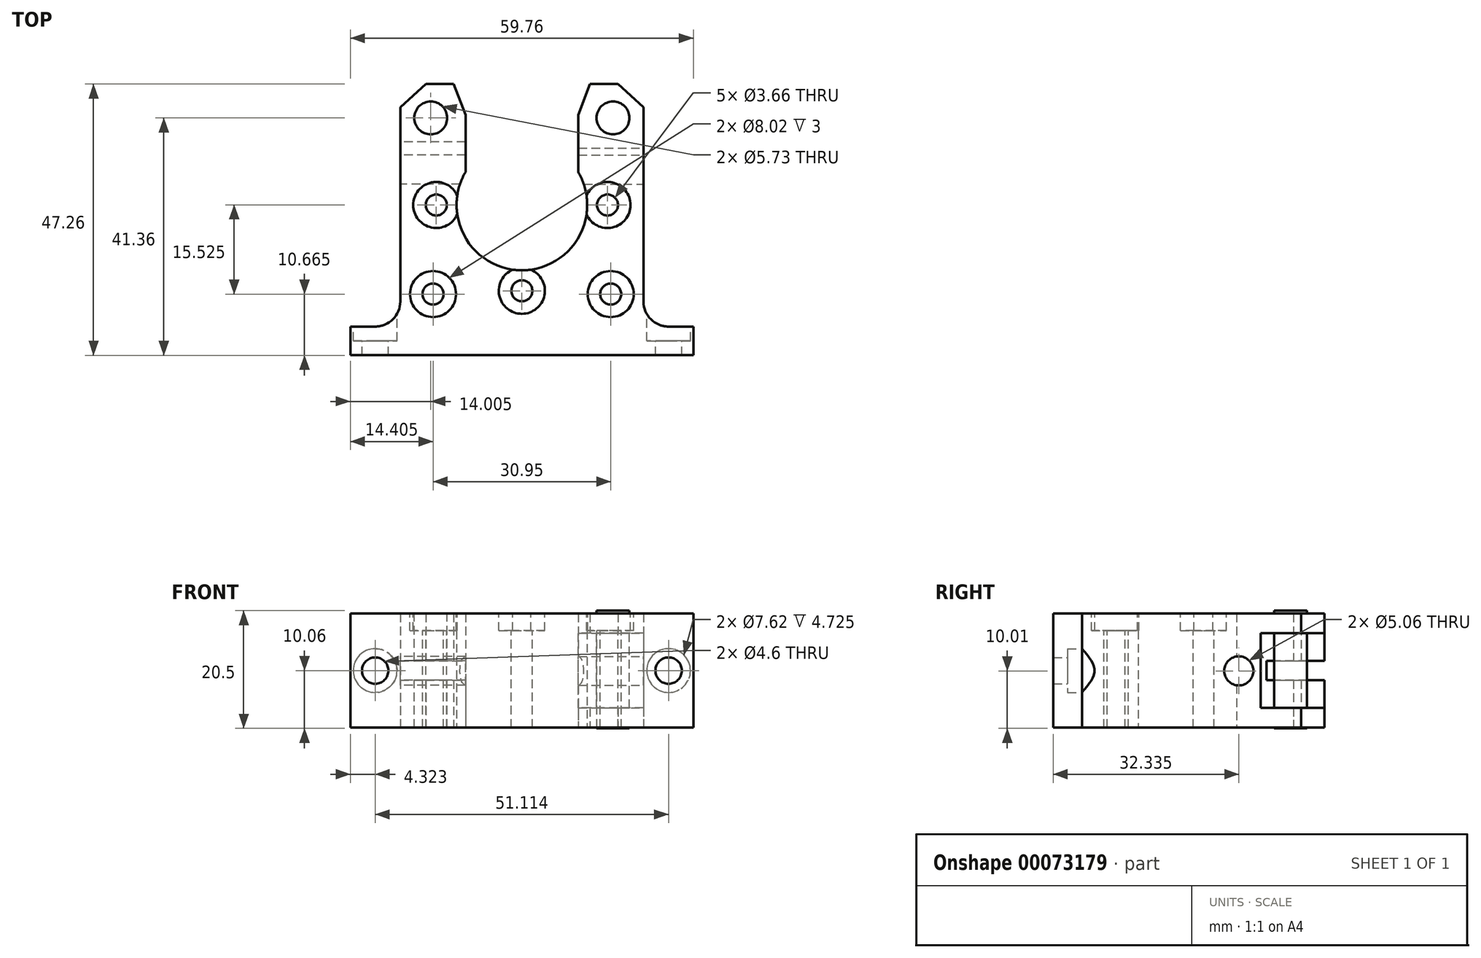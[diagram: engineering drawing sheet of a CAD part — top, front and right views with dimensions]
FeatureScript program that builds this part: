
annotation { "Feature Type Name" : "Feature", "Feature Type Description" : "" }
export const myFeature = defineFeature(function(context is Context, id is Id, definition is map)
    precondition{}
    {
        {
            var Q0;
            Q0=qCreatedBy(makeId("Top.planeOp"),FACE);
            var sketch = newSketch(context, id + "F0", { "sketchPlane" : qUnion([Q0])});
            skLineSegment(sketch, "E0", {"start": v(0, -26.18) * mm, "end": v(29.88, -26.18) * mm});
            skLineSegment(sketch, "E1", {"start": v(29.88, -26.18) * mm, "end": v(29.88, -21.18) * mm});
            skLineSegment(sketch, "E2", {"start": v(29.88, -21.18) * mm, "end": v(21.18, -21.18) * mm});
            skLineSegment(sketch, "E3", {"start": v(21.18, -21.18) * mm, "end": v(21.18, 17.02) * mm});
            skLineSegment(sketch, "E4", {"start": v(21.18, 17.02) * mm, "end": v(16.73, 21.07) * mm});
            skLineSegment(sketch, "E5", {"start": v(16.73, 21.07) * mm, "end": v(11.88, 21.07) * mm});
            skLineSegment(sketch, "E6", {"start": v(11.88, 21.07) * mm, "end": v(9.82, 15.68) * mm});
            skLineSegment(sketch, "E7", {"start": v(9.83, 15.68) * mm, "end": v(9.83, 5.73) * mm});
            skArc(sketch, "E8", {"start": v(0, -11.38) * mm, "mid": v(9.86, -5.67) * mm, "end": v(9.83, 5.73) * mm});
            skPoint(sketch, "E9", {"position": v(9.83, 5.73) * mm});
            skPoint(sketch, "E10", {"position": v(9.83, -5.73) * mm});
            skPoint(sketch, "E11.end.orphan", {"position": v(0, -11.38) * mm});
            skLineSegment(sketch, "E12", {"start": v(0, -11.38) * mm, "end": v(0, -26.18) * mm});
            skSolve(sketch);
        }
        {
            var Q0;
            Q0 = qSketchRegion(id + "F0", true);
            extrude(context, id + "F1", {"entities" : qUnion([Q0]), "depth" : 19.88 * mm});
        }
        {
            var Q0;
            Q0=makeQuery(id+"F1.opExtrude","SWEPT_EDGE",EDGE,{"disambiguationData":[OSD([sQuery(id+"F0.wireOp",EDGE,"E2"),sQuery(id+"F0.wireOp",EDGE,"E3")])]});
            fillet(context, id + "F2", {"entities" : qUnion([Q0]), "radius" : 4.38 * mm, "tangentPropagation" : true, "allowEdgeOverflow" : false});
        }
        {
            var Q0;
            Q0=makeQuery(id+"F1.opExtrude","SWEPT_FACE",FACE,{"disambiguationData":[OSD([sQuery(id+"F0.wireOp",EDGE,"E2")])]});
            var sketch = newSketch(context, id + "F3", { "sketchPlane" : qUnion([Q0])});
            skCircle(sketch, "E13", {"center": v(-25.56, 9.94) * mm, "radius": 3.81 * mm});
            skSolve(sketch);
        }
        {
            var Q0;
            Q0 = qSketchRegion(id + "F3", true);
            extrude(context, id + "F4", {"entities" : qUnion([Q0]), "operationType" : NewBodyOperationType.REMOVE, "oppositeDirection" : true, "depth" : 2.5 * mm, "hasSecondDirection" : true, "secondDirectionOppositeDirection" : false, "secondDirectionDepth" : 5 * mm});
        }
        {
            var Q0;
            Q0=makeQuery(id+"F4.boolean.opBoolean","COPY",FACE,{"derivedFrom":makeQuery(id+"F4.opExtrude","CAP_FACE",FACE,{"disambiguationData":[OSD([sQuery(id+"F3.wireOp",EDGE,"E13")])],"isStart":false})});
            var sketch = newSketch(context, id + "F5", { "sketchPlane" : qUnion([Q0])});
            skCircle(sketch, "E14", {"center": v(-25.56, 9.94) * mm, "radius": 2.3 * mm});
            skSolve(sketch);
        }
        {
            var Q0;
            Q0 = qSketchRegion(id + "F5", true);
            extrude(context, id + "F6", {"entities" : qUnion([Q0]), "operationType" : NewBodyOperationType.REMOVE, "endBound" : BoundingType.THROUGH_ALL, "oppositeDirection" : true, "depth" : 25 * mm});
        }
        {
            var Q0;
            Q0=makeQuery(id+"F1.opExtrude","CAP_FACE",FACE,{"disambiguationData":[OSD([sQuery(id+"F0.wireOp",EDGE,"E0"),sQuery(id+"F0.wireOp",EDGE,"E1"),sQuery(id+"F0.wireOp",EDGE,"E2"),sQuery(id+"F0.wireOp",EDGE,"E3"),sQuery(id+"F0.wireOp",EDGE,"E4"),sQuery(id+"F0.wireOp",EDGE,"E5"),sQuery(id+"F0.wireOp",EDGE,"E6"),sQuery(id+"F0.wireOp",EDGE,"E7"),sQuery(id+"F0.wireOp",EDGE,"E8"),sQuery(id+"F0.wireOp",EDGE,"E12")])],"isStart":false});
            var sketch = newSketch(context, id + "F7", { "sketchPlane" : qUnion([Q0])});
            skCircle(sketch, "E15", {"center": v(15.48, -15.52) * mm, "radius": 4 * mm});
            skCircle(sketch, "E16", {"center": v(0, -14.96) * mm, "radius": 4 * mm});
            skCircle(sketch, "E17", {"center": v(14.92, 0) * mm, "radius": 4 * mm});
            skSolve(sketch);
        }
        {
            var Q0;
            Q0 = qSketchRegion(id + "F7", true);
            extrude(context, id + "F8", {"entities" : qUnion([Q0]), "operationType" : NewBodyOperationType.REMOVE, "oppositeDirection" : true, "depth" : 3 * mm});
        }
        {
            var Q0;
            Q0=makeQuery(id+"F1.opExtrude","CAP_FACE",FACE,{"disambiguationData":[OSD([sQuery(id+"F0.wireOp",EDGE,"E0"),sQuery(id+"F0.wireOp",EDGE,"E1"),sQuery(id+"F0.wireOp",EDGE,"E2"),sQuery(id+"F0.wireOp",EDGE,"E3"),sQuery(id+"F0.wireOp",EDGE,"E4"),sQuery(id+"F0.wireOp",EDGE,"E5"),sQuery(id+"F0.wireOp",EDGE,"E6"),sQuery(id+"F0.wireOp",EDGE,"E7"),sQuery(id+"F0.wireOp",EDGE,"E8"),sQuery(id+"F0.wireOp",EDGE,"E12")])],"isStart":false});
            var sketch = newSketch(context, id + "F9", { "sketchPlane" : qUnion([Q0])});
            skCircle(sketch, "E18", {"center": v(14.92, 0) * mm, "radius": 1.83 * mm});
            skCircle(sketch, "E19", {"center": v(15.48, -15.52) * mm, "radius": 1.83 * mm});
            skCircle(sketch, "E20", {"center": v(0, -14.96) * mm, "radius": 1.83 * mm});
            skSolve(sketch);
        }
        {
            var Q0;
            Q0 = qSketchRegion(id + "F9", true);
            extrude(context, id + "F10", {"entities" : qUnion([Q0]), "operationType" : NewBodyOperationType.REMOVE, "endBound" : BoundingType.THROUGH_ALL, "oppositeDirection" : true, "depth" : 25 * mm});
        }
        {
            var Q0;
            Q0=makeQuery(id+"F1.opExtrude","SWEPT_FACE",FACE,{"disambiguationData":[OSD([sQuery(id+"F0.wireOp",EDGE,"E3")])]});
            var sketch = newSketch(context, id + "F11", { "sketchPlane" : qUnion([Q0])});
            skCircle(sketch, "E21", {"center": v(6.15, 9.9) * mm, "radius": 2.53 * mm});
            skSolve(sketch);
        }
        {
            var Q0;
            Q0 = qSketchRegion(id + "F11", true);
            extrude(context, id + "F12", {"entities" : qUnion([Q0]), "operationType" : NewBodyOperationType.REMOVE, "endBound" : BoundingType.THROUGH_ALL, "oppositeDirection" : true, "depth" : 25 * mm});
        }
        {
            var Q0;
            Q0=makeQuery(id+"F1.opExtrude","SWEPT_BODY",BODY,{"disambiguationData":[OSD([sQuery(id+"F0.wireOp",EDGE,"E0"),sQuery(id+"F0.wireOp",EDGE,"E1"),sQuery(id+"F0.wireOp",EDGE,"E2"),sQuery(id+"F0.wireOp",EDGE,"E3"),sQuery(id+"F0.wireOp",EDGE,"E4"),sQuery(id+"F0.wireOp",EDGE,"E5"),sQuery(id+"F0.wireOp",EDGE,"E6"),sQuery(id+"F0.wireOp",EDGE,"E7"),sQuery(id+"F0.wireOp",EDGE,"E8"),sQuery(id+"F0.wireOp",EDGE,"E12")])]});
            var Q1;
            Q1=qCreatedBy(makeId("Right.planeOp"),FACE);
            mirror(context, id + "F13", {"operationType" : NewBodyOperationType.ADD, "entities" : qUnion([Q0]), "mirrorPlane" : qUnion([Q1])});
        }
        {
            var Q0;
            Q0=makeQuery(id+"F1.opExtrude","SWEPT_FACE",FACE,{"disambiguationData":[OSD([sQuery(id+"F0.wireOp",EDGE,"E3")])]});
            var sketch = newSketch(context, id + "F14", { "sketchPlane" : qUnion([Q0])});
            skLineSegment(sketch, "E22.bottom", {"start": v(9.93, 16.46) * mm, "end": v(22, 16.46) * mm});
            skLineSegment(sketch, "E22.top", {"start": v(9.93, 3.43) * mm, "end": v(22, 3.43) * mm});
            skLineSegment(sketch, "E22.left", {"start": v(9.93, 16.46) * mm, "end": v(9.93, 3.43) * mm});
            skLineSegment(sketch, "E22.right", {"start": v(22, 16.46) * mm, "end": v(22, 3.43) * mm});
            skSolve(sketch);
        }
        {
            var Q0;
            Q0 = qSketchRegion(id + "F14", true);
            extrude(context, id + "F15", {"entities" : qUnion([Q0]), "operationType" : NewBodyOperationType.REMOVE, "endBound" : BoundingType.UP_TO_NEXT, "oppositeDirection" : true, "depth" : 25 * mm});
        }
        {
            var Q0;
            Q0=makeQuery(id+"F13.opPattern","COPY",FACE,{"derivedFrom":makeQuery(id+"F1.opExtrude","SWEPT_FACE",FACE,{"disambiguationData":[OSD([sQuery(id+"F0.wireOp",EDGE,"E3")])]}),"instanceName":"1"});
            var sketch = newSketch(context, id + "F16", { "sketchPlane" : qUnion([Q0])});
            skLineSegment(sketch, "E23.bottom", {"start": v(-10.97, 8.26) * mm, "end": v(-21.47, 8.26) * mm});
            skLineSegment(sketch, "E23.top", {"start": v(-10.97, 11.62) * mm, "end": v(-21.47, 11.62) * mm});
            skLineSegment(sketch, "E23.left", {"start": v(-10.97, 8.26) * mm, "end": v(-10.97, 11.62) * mm});
            skLineSegment(sketch, "E23.right", {"start": v(-21.47, 8.26) * mm, "end": v(-21.47, 11.62) * mm});
            skSolve(sketch);
        }
        {
            var Q0;
            Q0 = qSketchRegion(id + "F16", true);
            extrude(context, id + "F17", {"entities" : qUnion([Q0]), "operationType" : NewBodyOperationType.REMOVE, "endBound" : BoundingType.UP_TO_NEXT, "oppositeDirection" : true, "depth" : 25 * mm});
        }
        {
            var Q0;
            {var subQ0=makeQuery(id+"F1.opExtrude","CAP_FACE",FACE,{"disambiguationData":[OSD([sQuery(id+"F0.wireOp",EDGE,"E0"),sQuery(id+"F0.wireOp",EDGE,"E1"),sQuery(id+"F0.wireOp",EDGE,"E2"),sQuery(id+"F0.wireOp",EDGE,"E3"),sQuery(id+"F0.wireOp",EDGE,"E4"),sQuery(id+"F0.wireOp",EDGE,"E5"),sQuery(id+"F0.wireOp",EDGE,"E6"),sQuery(id+"F0.wireOp",EDGE,"E7"),sQuery(id+"F0.wireOp",EDGE,"E8"),sQuery(id+"F0.wireOp",EDGE,"E12")])],"isStart":false});Q0=makeQuery(id+"F13.boolean.opBoolean","MERGE",FACE,{"derivedFrom":[subQ0,makeQuery(id+"F13.opPattern","COPY",FACE,{"derivedFrom":subQ0,"instanceName":"1"})]});}
            var sketch = newSketch(context, id + "F18", { "sketchPlane" : qUnion([Q0])});
            skCircle(sketch, "E24", {"center": v(15.88, 15.17) * mm, "radius": 2.87 * mm});
            skSolve(sketch);
        }
        {
            var Q0;
            Q0 = qSketchRegion(id + "F18", true);
            extrude(context, id + "F19", {"entities" : qUnion([Q0]), "operationType" : NewBodyOperationType.ADD, "oppositeDirection" : true, "depth" : 20 * mm, "hasSecondDirection" : true, "secondDirectionOppositeDirection" : false, "secondDirectionDepth" : 0.5 * mm});
        }
        {
            var Q0;
            {var subQ0=makeQuery(id+"F1.opExtrude","CAP_FACE",FACE,{"disambiguationData":[OSD([sQuery(id+"F0.wireOp",EDGE,"E0"),sQuery(id+"F0.wireOp",EDGE,"E1"),sQuery(id+"F0.wireOp",EDGE,"E2"),sQuery(id+"F0.wireOp",EDGE,"E3"),sQuery(id+"F0.wireOp",EDGE,"E4"),sQuery(id+"F0.wireOp",EDGE,"E5"),sQuery(id+"F0.wireOp",EDGE,"E6"),sQuery(id+"F0.wireOp",EDGE,"E7"),sQuery(id+"F0.wireOp",EDGE,"E8"),sQuery(id+"F0.wireOp",EDGE,"E12")])],"isStart":false});Q0=makeQuery(id+"F13.boolean.opBoolean","MERGE",FACE,{"derivedFrom":[subQ0,makeQuery(id+"F13.opPattern","COPY",FACE,{"derivedFrom":subQ0,"instanceName":"1"})]});}
            var sketch = newSketch(context, id + "F20", { "sketchPlane" : qUnion([Q0])});
            skCircle(sketch, "E25", {"center": v(-15.88, 15.17) * mm, "radius": 2.87 * mm});
            skSolve(sketch);
        }
        {
            var Q0;
            Q0 = qSketchRegion(id + "F20", true);
            extrude(context, id + "F21", {"entities" : qUnion([Q0]), "operationType" : NewBodyOperationType.REMOVE, "endBound" : BoundingType.THROUGH_ALL, "oppositeDirection" : true, "depth" : 25 * mm});
        }
    });
